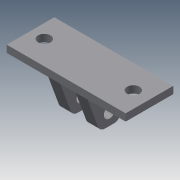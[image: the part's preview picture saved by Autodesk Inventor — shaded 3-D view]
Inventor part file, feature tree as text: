
AUTODESK INVENTOR PART (.ipt)
format: ipt  version: 2016 (Build 200138000, 138)  size: 138,240 bytes
history: native  units: in
note: dims shown in document units (in); Inventor stores cm internally (conversion verified against a paired STEP export)
features: extrude x3, sketch x3, fillet x1, draft x1
ambient origin geometry x8: Origin, YZ Plane, XZ Plane, XY Plane, X Axis, Y Axis, Z Axis, Center Point
bodies: Solid1 (feature_tree)
feature tree (8):
  extrude  "Extrusion1"  Depth=0.7874in
  extrude  "Extrusion2"  Depth=0.2047in
  fillet  "Fillet1"  Radius=0.26in
  draft  "FaceDraft1"
  extrude  "Extrusion3"  Depth=0.1969in
  sketch  "Sketch1"  dims[d0=1.9685in d1=0.7874in]
  sketch  "Sketch2"  dims[d2=0.2047in d3=0.2047in d4=0.26in]
  sketch  "Sketch3"  dims[d5=0.1969in d6=0.1969in d7=0.1181in d8=0.0in d9=0.1969in d10=0.1969in d11=0.256in d12=0.13in d13=0.1969in d14=0.1969in d15=0.5906in d16=0.0in d17=0.125in d18=0.1374in d19=0.1875in d20=0.2in d21=0.5906in d22=0.0in]
